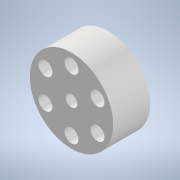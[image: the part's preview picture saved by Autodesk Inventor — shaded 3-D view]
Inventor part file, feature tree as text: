
AUTODESK INVENTOR PART (.ipt)
format: ipt  version: 2021 (Build 250183000, 183)  size: 123,904 bytes
history: native  units: mm
features: extrude x3, sketch x3, other x3, reference x1
ambient origin geometry x8: Origin, YZ Plane, XZ Plane, XY Plane, X Axis, Y Axis, Z Axis, Center Point
bodies: Solid1 (feature_tree)
feature tree (10):
  extrude  "Extrusion1"  Depth=3.0mm TaperAngle=0.0deg
  extrude  "Extrusion2"  Depth=3.0mm
  extrude  "Extrusion3"  TaperAngle=0.0deg  [1 undecoded]
  sketch  "Sketch1"  dims[d0=18.0mm d1=3.0mm d2=5.0mm d3=0.0mm d4=0.0mm]
  reference  "Reference1"
  sketch  "Sketch2"  dims[d5=13.0mm d6=3.0mm]
  sketch  "Sketch3"  dims[d7=60.0mm d9=360.0deg d11=0.0mm d12=0.0mm d13=2.5mm d14=0.0mm d15=0.0mm]
  parser-record x1  (decoder bookkeeping rows leaked as tree rows — omitted from the tree; the rows remain in map.json)
  other  "ilmbt_3d_v1.iam"
  other  "servo_shaft:1"
note: 1 required parameter value undecoded (feature->parameter linkage not recoverable at this tier; creation-order binding heuristic only, values carry confidence <= 0.55)
note: 1 file-system path scrubbed to <path> (originals preserved in map.json)
